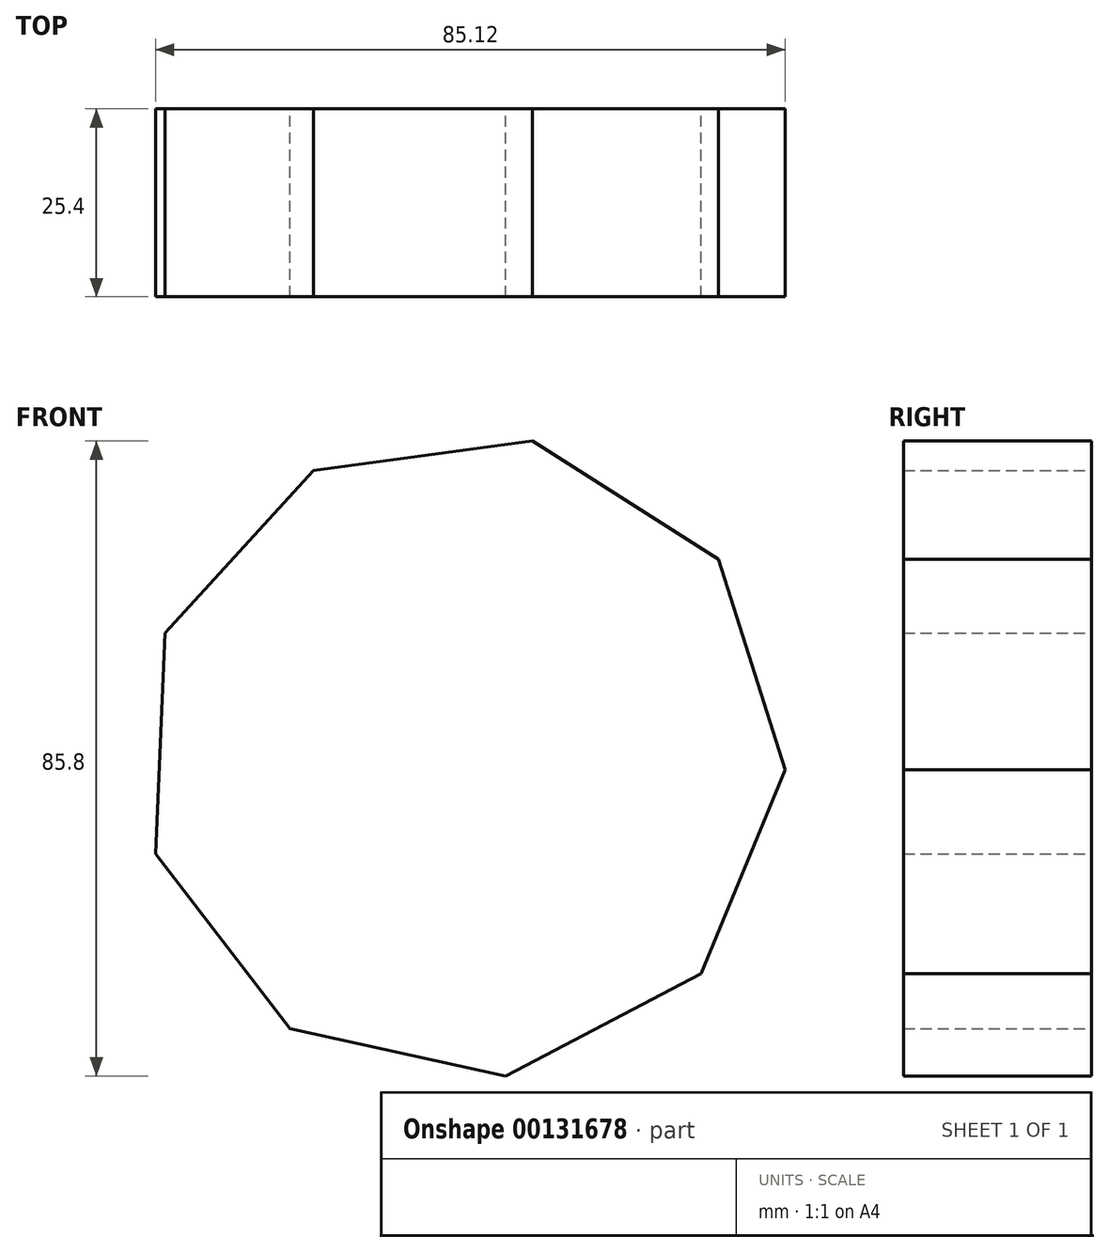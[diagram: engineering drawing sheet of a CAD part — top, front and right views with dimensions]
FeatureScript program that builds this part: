
annotation { "Feature Type Name" : "Feature", "Feature Type Description" : "" }
export const myFeature = defineFeature(function(context is Context, id is Id, definition is map)
    precondition{}
    {
        {
            var Q0;
            Q0=qCreatedBy(makeId("Front.planeOp"),FACE);
            var sketch = newSketch(context, id + "F0", { "sketchPlane" : qUnion([Q0])});
            skCircle(sketch, "E0.cCircle", {"center": v(0, 0) * mm, "radius": 40.97 * mm, "construction": true});
            skLineSegment(sketch, "E0.0", {"start": v(-40.3, 16.62) * mm, "end": v(-20.2, 38.64) * mm});
            skLineSegment(sketch, "E0.1", {"start": v(-20.2, 38.64) * mm, "end": v(9.37, 42.58) * mm});
            skLineSegment(sketch, "E0.2", {"start": v(9.37, 42.58) * mm, "end": v(34.54, 26.6) * mm});
            skLineSegment(sketch, "E0.3", {"start": v(34.54, 26.6) * mm, "end": v(43.56, -1.83) * mm});
            skLineSegment(sketch, "E0.4", {"start": v(43.56, -1.83) * mm, "end": v(32.2, -29.4) * mm});
            skLineSegment(sketch, "E0.5", {"start": v(32.2, -29.4) * mm, "end": v(5.76, -43.22) * mm});
            skLineSegment(sketch, "E0.6", {"start": v(5.76, -43.22) * mm, "end": v(-23.36, -36.8) * mm});
            skLineSegment(sketch, "E0.7", {"start": v(-23.36, -36.8) * mm, "end": v(-41.56, -13.18) * mm});
            skLineSegment(sketch, "E0.8", {"start": v(-41.56, -13.18) * mm, "end": v(-40.3, 16.62) * mm});
            skPoint(sketch, "E0.0.midPoint", {"position": v(-30.25, 27.63) * mm});
            skSolve(sketch);
        }
        {
            var Q0;
            Q0 = qSketchRegion(id + "F0", true);
            extrude(context, id + "F1", {"entities" : qUnion([Q0]), "depth" : 25.4 * mm});
        }
    });
